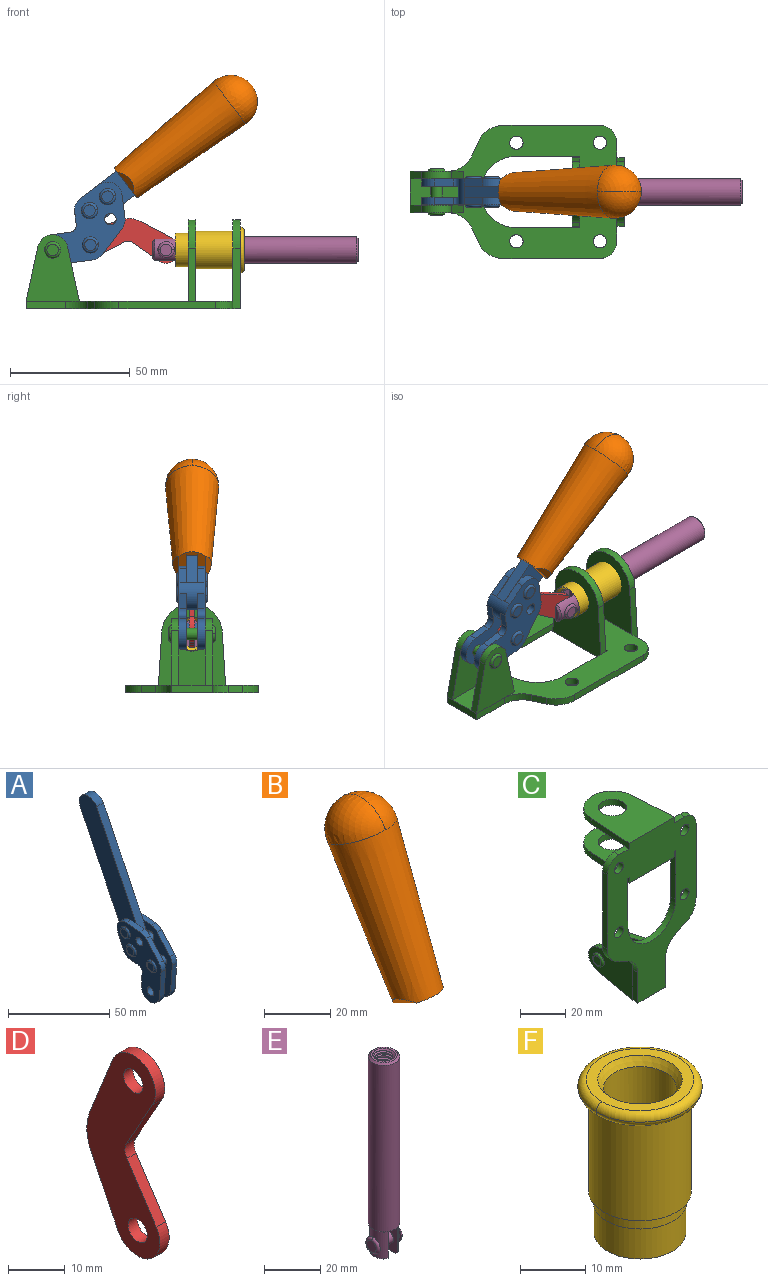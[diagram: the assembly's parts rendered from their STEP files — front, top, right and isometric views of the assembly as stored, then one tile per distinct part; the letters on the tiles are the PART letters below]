
ASSEMBLY  parts=6 mates=6
PART A: 59 faces, bbox 12.9x60.2x99.6 mm
  f0: torus R=2.39mm, axis (-1,0,0), area 14.9mm2, adj f20,f43,f51
  f1: torus R=2.39mm, axis (-1,0,0), area 14.9mm2, adj f19,f42,f51
  f2: torus R=2.39mm, axis (-1,0,0), area 14.9mm2, adj f18,f35,f51
  f3: torus R=2.39mm, axis (-1,0,0), area 14.9mm2, adj f14,f17,f23
  f4: torus R=2.39mm, axis (-1,0,0), area 14.9mm2, adj f13,f16,f23
  f5: torus R=2.39mm, axis (-1,0,0), area 14.9mm2, adj f12,f15,f23
  f6: cylinder r=2.39mm len=4.78mm, axis (1,0,0), area 46.5mm2, adj f48,f50,f51
  f7: cylinder r=2.39mm len=4.78mm, axis (1,0,0), area 46.5mm2, adj f50,f51
  f8: cylinder r=6.35mm len=12.68mm, axis (1,0,0), area 61.8mm2, adj f38,f39,f50,f51
  f9: cylinder r=2.39mm len=4.78mm, axis (-1,0,0), area 70.5mm2, adj f46,f50
  f10: cylinder r=2.39mm len=4.78mm, axis (-1,0,0), area 46.5mm2, adj f23,f45,f46
  f11: cylinder r=2.39mm len=4.78mm, axis (-1,0,0), area 46.5mm2, adj f23,f46
  f12: plane 4.78x4.78mm, normal (1,0,0), area 17.9mm2, adj f5,f15
  f13: plane 4.78x4.78mm, normal (1,0,0), area 17.9mm2, adj f4,f16
  f14: plane 4.78x4.78mm, normal (1,0,0), area 17.9mm2, adj f3,f17
  f15: torus R=2.39mm, axis (-1,0,0), area 14.9mm2, adj f5,f12,f23
  f16: torus R=2.39mm, axis (-1,0,0), area 14.9mm2, adj f4,f13,f23
  f17: torus R=2.39mm, axis (-1,0,0), area 14.9mm2, adj f3,f14,f23
  f18: plane 4.78x4.78mm, normal (-1,0,0), area 17.9mm2, adj f2,f35
  f19: plane 4.78x4.78mm, normal (-1,0,0), area 17.9mm2, adj f1,f42
  f20: plane 4.78x4.78mm, normal (-1,0,0), area 17.9mm2, adj f0,f43
  f21: plane 2.26x0.2mm, normal (1,0,0), area 0.2mm2, adj f31,f44
  f22: plane 2.26x0.2mm, normal (-1,0,0), area 0.2mm2, adj f41,f44
  f23: plane 39.37x30.77mm, normal (1,0,0), area 565.5mm2, adj f3,f4,f5,f10,f11,f15,f16,f17
  f24: cylinder r=6.1mm len=4.15mm, axis (-1,0,0), area 14.7mm2, adj f23,f25,f32,f46
  f25: plane 10.25x9.01mm, normal (0,-0.75,0.66), area 42.3mm2, adj f23,f24,f26,f46
  f26: cylinder r=6.35mm len=4.64mm, axis (-1,0,0), area 15.6mm2, adj f23,f25,f27,f46
  f27: plane 15.84x3.1mm, normal (0,-1,-0.07), area 49.2mm2, adj f23,f26,f28,f46
  f28: cylinder r=6.35mm len=12.68mm, axis (-1,0,0), area 61.8mm2, adj f23,f27,f29,f46
  f29: plane 8.11x3.1mm, normal (0,1,0.07), area 25.2mm2, adj f23,f28,f30,f46
  f30: cylinder r=3.05mm len=3.25mm, axis (-1,0,0), area 14.8mm2, adj f23,f29,f31,f46
  f31: plane 5.99x3.1mm, normal (0,0.07,-1), area 18.6mm2, adj f21,f23,f30,f44,f46
  f32: plane 9.5x3.1mm, normal (0,-0.07,1), area 29.5mm2, adj f23,f24,f33,f46,f47
  f33: cylinder r=6.1mm len=8.63mm, axis (-1,0,0), area 39.1mm2, adj f23,f32,f34,f47
  f34: plane 8.65x3.96mm, normal (0,0.91,-0.42), area 29.5mm2, adj f23,f33,f44,f47
  f35: torus R=2.39mm, axis (-1,0,0), area 14.9mm2, adj f2,f18,f51
  f36: plane 10.25x9.01mm, normal (0,-0.75,0.66), area 42.3mm2, adj f37,f49,f50,f51
  f37: cylinder r=6.35mm len=4.64mm, axis (1,0,0), area 15.6mm2, adj f36,f38,f50,f51
  f38: plane 15.84x3.1mm, normal (0,-1,-0.07), area 49.2mm2, adj f8,f37,f50,f51
  f39: plane 8.11x3.1mm, normal (0,1,0.07), area 25.2mm2, adj f8,f40,f50,f51
  f40: cylinder r=3.05mm len=3.25mm, axis (1,0,0), area 14.8mm2, adj f39,f41,f50,f51
  f41: plane 5.99x3.1mm, normal (0,0.07,-1), area 18.6mm2, adj f22,f40,f44,f50,f51
  f42: torus R=2.39mm, axis (-1,0,0), area 14.9mm2, adj f1,f19,f51
  f43: torus R=2.39mm, axis (-1,0,0), area 14.9mm2, adj f0,f20,f51
  f44: cylinder r=6.35mm len=12.12mm, axis (-1,0,0), area 128.9mm2, adj f21,f22,f23,f31,f34,f41,f46,f47
  f45: plane 2.65x1.35mm, normal (1,0,0), area 1mm2, adj f10,f55
  f46: plane 39.08x20.42mm, normal (-1,0,0), area 412.5mm2, adj f9,f10,f11,f24,f25,f26,f27,f28
  f47: plane 77.62x39.82mm, normal (1,0,0), area 850mm2, adj f32,f33,f34,f44,f53,f54,f55
  f48: plane 2.65x1.35mm, normal (-1,0,0), area 1mm2, adj f6,f55
  f49: cylinder r=6.1mm len=4.15mm, axis (1,0,0), area 14.7mm2, adj f36,f50,f51,f56
  f50: plane 39.08x20.42mm, normal (1,0,0), area 412.5mm2, adj f6,f7,f8,f9,f36,f37,f38,f39
  f51: plane 39.37x30.77mm, normal (-1,0,0), area 565.5mm2, adj f0,f1,f2,f6,f7,f8,f35,f36
  f52: plane 8.65x3.96mm, normal (0,0.91,-0.42), area 29.5mm2, adj f44,f51,f57,f58
  f53: plane 68.49x33.4mm, normal (0,0.9,-0.44), area 358.1mm2, adj f44,f47,f54,f58
  f54: cylinder r=6.35mm len=12.06mm, axis (1,0,0), area 93.7mm2, adj f47,f53,f55,f58
  f55: plane 68.49x33.4mm, normal (0,-0.9,0.44), area 358.1mm2, adj f44,f45,f46,f47,f48,f50,f54,f58
  f56: plane 9.5x3.1mm, normal (0,-0.07,1), area 29.5mm2, adj f49,f50,f51,f57,f58
  f57: cylinder r=6.1mm len=8.63mm, axis (1,0,0), area 39.1mm2, adj f51,f52,f56,f58
  f58: plane 77.62x39.82mm, normal (-1,0,0), area 850mm2, adj f44,f52,f53,f54,f55,f56,f57
PART B: 11 faces, bbox 22.3x42.6x64.5 mm
  f0: sphere r=11.13mm, area 411.4mm2, adj f1,f8
  f1: cone r=11.11mm half-angle=3.3deg, axis (0,0.44,0.9), area 3251.8mm2, adj f0,f7,f8,f9,f10
  f2: cylinder r=6.16mm len=11.7mm, axis (1,0,0), area 89.5mm2, adj f3,f4,f5,f6
  f3: plane 60.23x36.75mm, normal (-1,0,0), area 763.6mm2, adj f2,f4,f6,f10
  f4: plane 51.37x25.05mm, normal (0,0.9,-0.44), area 264.2mm2, adj f2,f3,f5,f10
  f5: plane 60.23x36.75mm, normal (1,0,0), area 763.6mm2, adj f2,f4,f6,f10
  f6: plane 51.37x25.05mm, normal (0,-0.9,0.44), area 264.2mm2, adj f2,f3,f5,f10
  f7: plane 9.95x5.95mm, normal (0.71,-0.31,-0.64), area 25.8mm2, adj f1,f10
  f8: sphere r=11.13mm, area 411.4mm2, adj f0,f1
  f9: plane 9.95x5.95mm, normal (-0.71,-0.31,-0.64), area 25.8mm2, adj f1,f10
  f10: plane 14.27x11.38mm, normal (0,-0.44,-0.9), area 106.7mm2, adj f1,f3,f4,f5,f6,f7,f9
PART C: 55 faces, bbox 55.7x37.4x89.8 mm
  f0: torus R=2.41mm, axis (-1,0,0), area 15mm2, adj f11,f15,f25
  f1: torus R=2.41mm, axis (-1,0,0), area 15mm2, adj f10,f12,f22
  f2: cylinder r=2.78mm len=5.56mm, axis (0,-1,0), area 54.2mm2, adj f30,f54
  f3: cylinder r=14.99mm len=29.97mm, axis (0,-1,0), area 145.9mm2, adj f30,f49,f53,f54
  f4: cylinder r=2.78mm len=5.56mm, axis (0,-1,0), area 54.2mm2, adj f30,f54
  f5: cylinder r=2.78mm len=5.56mm, axis (0,-1,0), area 54.2mm2, adj f30,f54
  f6: cylinder r=2.78mm len=5.56mm, axis (0,-1,0), area 54.2mm2, adj f30,f54
  f7: cylinder r=6.35mm len=12.7mm, axis (0,0,1), area 123.6mm2, adj f27,f51
  f8: cylinder r=6.35mm len=12.7mm, axis (0,0,-1), area 124.7mm2, adj f21,f35
  f9: cylinder r=2.41mm len=11.18mm, axis (-1,0,0), area 169.4mm2, adj f16,f19
  f10: plane 4.83x4.83mm, normal (1,0,0), area 18.3mm2, adj f1,f12
  f11: plane 4.83x4.83mm, normal (-1,0,0), area 18.3mm2, adj f0,f15
  f12: torus R=2.41mm, axis (-1,0,0), area 15mm2, adj f1,f10,f22
  f13: cylinder r=6.35mm len=12.41mm, axis (1,0,0), area 53.4mm2, adj f18,f19,f22,f23
  f14: cylinder r=6.35mm len=12.41mm, axis (-1,0,0), area 53.4mm2, adj f16,f17,f24,f25
  f15: torus R=2.41mm, axis (-1,0,0), area 15mm2, adj f0,f11,f25
  f16: plane 27.86x22.35mm, normal (1,0,0), area 425.4mm2, adj f9,f14,f17,f24,f30
  f17: plane 22.86x4.97mm, normal (0,0.21,0.98), area 72.5mm2, adj f14,f16,f25,f30
  f18: plane 22.86x4.97mm, normal (0,0.21,0.98), area 72.5mm2, adj f13,f19,f22,f30
  f19: plane 27.86x22.35mm, normal (-1,0,0), area 425.4mm2, adj f9,f13,f18,f23,f30
  f20: cylinder r=12.7mm len=25.35mm, axis (0,0,-1), area 119.8mm2, adj f21,f34,f35,f36
  f21: plane 34.21x28.07mm, normal (0,0,-1), area 702.4mm2, adj f8,f20,f30,f34,f36
  f22: plane 27.96x22.45mm, normal (1,0,0), area 407.2mm2, adj f1,f12,f13,f18,f23,f30,f42,f43
  f23: plane 22.86x4.97mm, normal (0,0.21,-0.98), area 72.5mm2, adj f13,f19,f22,f44
  f24: plane 22.86x4.97mm, normal (0,0.21,-0.98), area 72.5mm2, adj f14,f16,f25,f44
  f25: plane 27.86x22.35mm, normal (-1,0,0), area 407.1mm2, adj f0,f14,f15,f17,f24,f30,f45,f46
  f26: plane 3.1x0.95mm, normal (0,0,-1), area 2.7mm2, adj f30,f49,f50,f54
  f27: plane 34.21x28.07mm, normal (0,0,1), area 702.4mm2, adj f7,f28,f30,f50,f52
  f28: cylinder r=12.7mm len=25.35mm, axis (0,0,1), area 118.8mm2, adj f27,f50,f51,f52
  f29: plane 3.1x0.95mm, normal (0,0,-1), area 2.7mm2, adj f30,f52,f53,f54
  f30: plane 86.54x55.63mm, normal (0,1,0), area 2362.9mm2, adj f2,f3,f4,f5,f6,f16,f17,f18
  f31: plane 40.56x3.1mm, normal (-1,0,0), area 125.7mm2, adj f30,f32,f48,f54
  f32: cylinder r=7.11mm len=7.11mm, axis (0,-1,0), area 34.6mm2, adj f30,f31,f33,f54
  f33: plane 6.67x3.1mm, normal (0,0,1), area 20.4mm2, adj f30,f32,f34,f54
  f34: plane 25.39x3.13mm, normal (-1,0.06,0), area 79.5mm2, adj f20,f21,f33,f35,f54
  f35: plane 37.31x28.45mm, normal (0,0,1), area 789.9mm2, adj f8,f20,f34,f36,f54
  f36: plane 25.39x3.13mm, normal (1,0.06,0), area 79.5mm2, adj f20,f21,f35,f37,f54
  f37: plane 6.67x3.1mm, normal (0,0,1), area 20.4mm2, adj f30,f36,f38,f54
  f38: cylinder r=7.11mm len=7.11mm, axis (0,-1,0), area 34.6mm2, adj f30,f37,f39,f54
  f39: plane 40.56x3.1mm, normal (1,0,0), area 125.7mm2, adj f30,f38,f40,f54
  f40: cylinder r=11.18mm len=10.16mm, axis (0,-1,0), area 39.5mm2, adj f30,f39,f41,f54
  f41: plane 6.09x3.1mm, normal (0.42,0,-0.91), area 20.8mm2, adj f30,f40,f42,f54
  f42: cylinder r=11.18mm len=9.41mm, axis (0,-1,0), area 37.2mm2, adj f22,f30,f41,f43,f54
  f43: plane 16.5x3.1mm, normal (1,0,0), area 51.1mm2, adj f22,f42,f44,f54
  f44: plane 17.37x3.1mm, normal (0,0,-1), area 53.8mm2, adj f23,f24,f30,f43,f45,f54
  f45: plane 16.5x3.1mm, normal (-1,0,0), area 51.1mm2, adj f25,f44,f46,f54
  f46: cylinder r=11.18mm len=9.41mm, axis (0,-1,0), area 37.2mm2, adj f25,f30,f45,f47,f54
  f47: plane 6.09x3.1mm, normal (-0.42,0,-0.91), area 20.8mm2, adj f30,f46,f48,f54
  f48: cylinder r=11.18mm len=10.16mm, axis (0,-1,0), area 39.5mm2, adj f30,f31,f47,f54
  f49: plane 26.54x3.1mm, normal (-1,0,0), area 82.3mm2, adj f3,f26,f30,f54
  f50: plane 25.39x3.1mm, normal (1,0.06,0), area 78.8mm2, adj f26,f27,f28,f51,f54
  f51: plane 37.31x28.45mm, normal (0,0,-1), area 789.9mm2, adj f7,f28,f50,f52,f54
  f52: plane 25.39x3.1mm, normal (-1,0.06,0), area 78.8mm2, adj f27,f28,f29,f51,f54
  f53: plane 26.54x3.1mm, normal (1,0,0), area 82.3mm2, adj f3,f29,f30,f54
  f54: plane 89.66x55.63mm, normal (0,-1,0), area 2678.5mm2, adj f2,f3,f4,f5,f6,f26,f29,f31
PART D: 12 faces, bbox 2.3x18.2x42.8 mm
  f0: cylinder r=2.4mm len=4.8mm, axis (1,0,0), area 34.9mm2, adj f4,f11
  f1: cylinder r=10.41mm len=8.47mm, axis (1,0,0), area 20.2mm2, adj f4,f9,f10,f11
  f2: cylinder r=3.05mm len=3.16mm, axis (1,0,0), area 7.7mm2, adj f4,f6,f7,f11
  f3: cylinder r=2.4mm len=4.8mm, axis (1,0,0), area 34.9mm2, adj f4,f11
  f4: plane 42.81x18.23mm, normal (-1,0,0), area 414.1mm2, adj f0,f1,f2,f3,f5,f6,f7,f8
  f5: cylinder r=5.54mm len=10.67mm, axis (1,0,0), area 41.8mm2, adj f4,f6,f10,f11
  f6: plane 11.66x6.53mm, normal (0,-0.87,-0.49), area 30.9mm2, adj f2,f4,f5,f11
  f7: plane 11.17x7.33mm, normal (0,-0.84,0.55), area 30.9mm2, adj f2,f4,f8,f11
  f8: cylinder r=5.54mm len=10.51mm, axis (1,0,0), area 41.8mm2, adj f4,f7,f9,f11
  f9: plane 13.67x6.67mm, normal (0,0.9,-0.44), area 35.1mm2, adj f1,f4,f8,f11
  f10: plane 14.1x5.7mm, normal (0,0.93,0.37), area 35.1mm2, adj f1,f4,f5,f11
  f11: plane 42.81x18.23mm, normal (1,0,0), area 414.1mm2, adj f0,f1,f2,f3,f5,f6,f7,f8
PART E: 48 faces, bbox 12.6x11.1x86.1 mm
  f0: torus R=2.41mm, axis (-1,0,0), area 15mm2, adj f30,f32,f34
  f1: torus R=2.41mm, axis (-1,0,0), area 15mm2, adj f29,f31,f33
  f2: cylinder r=5.54mm len=72.39mm, axis (0,0,1), area 2518.5mm2, adj f3,f4,f42,f43
  f3: cone r=5.54mm half-angle=45deg, axis (0,0,1), area 7.6mm2, adj f2,f5,f41
  f4: cone r=5.54mm half-angle=45deg, axis (0,0,-1), area 34.9mm2, adj f2,f39
  f5: cylinder r=5.08mm len=11.48mm, axis (0,0,1), area 108.3mm2, adj f3,f7,f8,f41
  f6: cylinder r=2.41mm len=4.83mm, axis (-1,0,0), area 71.2mm2, adj f40,f41
  f7: cylinder r=2.41mm len=4.83mm, axis (-1,0,0), area 7.6mm2, adj f5,f34
  f8: cone r=5.08mm half-angle=45deg, axis (0,0,1), area 10.6mm2, adj f5,f37,f41
  f9: cone r=3.98mm half-angle=45deg, axis (0,0,1), area 17.6mm2, adj f27,f39,f45,f46,f47
  f10: cylinder r=2.41mm len=4.83mm, axis (-1,0,0), area 7.6mm2, adj f33,f38
  f11: cylinder r=3.2mm len=6.4mm, axis (0,0,1), area 78.4mm2, adj f12,f28,f44,f45,f47
  f12: cylinder r=3.2mm len=6.4mm, axis (0,0,1), area 10.5mm2, adj f11,f13,f45,f47
  f13: cylinder r=3.2mm len=6.4mm, axis (0,0,1), area 10.5mm2, adj f12,f14,f45,f47
  f14: cylinder r=3.2mm len=6.4mm, axis (0,0,1), area 10.5mm2, adj f13,f15,f45,f47
  f15: cylinder r=3.2mm len=6.4mm, axis (0,0,1), area 10.5mm2, adj f14,f16,f45,f47
  f16: cylinder r=3.2mm len=6.4mm, axis (0,0,1), area 10.5mm2, adj f15,f17,f45,f47
  f17: cylinder r=3.2mm len=6.4mm, axis (0,0,1), area 10.5mm2, adj f16,f18,f45,f47
  f18: cylinder r=3.2mm len=6.4mm, axis (0,0,1), area 10.5mm2, adj f17,f19,f45,f47
  f19: cylinder r=3.2mm len=6.4mm, axis (0,0,1), area 10.5mm2, adj f18,f20,f45,f47
  f20: cylinder r=3.2mm len=6.4mm, axis (0,0,1), area 10.5mm2, adj f19,f21,f45,f47
  f21: cylinder r=3.2mm len=6.4mm, axis (0,0,1), area 10.5mm2, adj f20,f22,f45,f47
  f22: cylinder r=3.2mm len=6.4mm, axis (0,0,1), area 10.5mm2, adj f21,f23,f45,f47
  f23: cylinder r=3.2mm len=6.4mm, axis (0,0,1), area 10.5mm2, adj f22,f24,f45,f47
  f24: cylinder r=3.2mm len=6.4mm, axis (0,0,1), area 10.5mm2, adj f23,f25,f45,f47
  f25: cylinder r=3.2mm len=6.4mm, axis (0,0,1), area 10.5mm2, adj f24,f26,f45,f47
  f26: cylinder r=3.2mm len=6.4mm, axis (0,0,1), area 10.5mm2, adj f25,f27,f45,f47
  f27: cylinder r=3.2mm len=6.4mm, axis (0,0,1), area 7.4mm2, adj f9,f26,f45,f47
  f28: cone r=3.2mm half-angle=60deg, axis (0,0,1), area 37.2mm2, adj f11
  f29: plane 4.83x4.83mm, normal (-1,0,0), area 18.3mm2, adj f1,f31
  f30: plane 4.83x4.83mm, normal (1,0,0), area 18.3mm2, adj f0,f32
  f31: torus R=2.41mm, axis (-1,0,0), area 15mm2, adj f1,f29,f33
  f32: torus R=2.41mm, axis (-1,0,0), area 15mm2, adj f0,f30,f34
  f33: plane 6.83x6.83mm, normal (1,0,0), area 18.3mm2, adj f1,f10,f31
  f34: plane 6.83x6.83mm, normal (-1,0,0), area 18.3mm2, adj f0,f7,f32
  f35: cone r=5.08mm half-angle=45deg, axis (0,0,1), area 10.6mm2, adj f36,f38,f40
  f36: plane 7.25x1.97mm, normal (0,0,-1), area 10mm2, adj f35,f40
  f37: plane 7.25x1.97mm, normal (0,0,-1), area 10mm2, adj f8,f41
  f38: cylinder r=5.08mm len=11.48mm, axis (0,0,1), area 108.3mm2, adj f10,f35,f40,f42
  f39: plane 9.55x9.55mm, normal (0,0,1), area 22mm2, adj f4,f9
  f40: plane 12.76x10.09mm, normal (1,0,0), area 95.7mm2, adj f6,f35,f36,f38,f42,f43
  f41: plane 12.76x10.09mm, normal (-1,0,0), area 95.7mm2, adj f3,f5,f6,f8,f37,f43
  f42: cone r=5.54mm half-angle=45deg, axis (0,0,1), area 7.6mm2, adj f2,f38,f40
  f43: plane 11.07x4.7mm, normal (0,0,-1), area 50.4mm2, adj f2,f40,f41
  f44: plane 0.89x0.62mm, normal (-1,0,0), area 0.3mm2, adj f11,f45,f46,f47
  f45: bspline ~24.8x7.63mm, area 266.6mm2, adj f9,f11,f12,f13,f14,f15,f16,f17
  f46: bspline ~24.87x7.63mm, area 73.6mm2, adj f9,f44,f45,f47
  f47: bspline ~24.98x7.63mm, area 272.5mm2, adj f9,f11,f12,f13,f14,f15,f16,f17
PART F: 15 faces, bbox 20.6x20.6x28.7 mm
  f0: torus R=8.26mm, axis (0,0,1), area 56.8mm2, adj f1,f10,f12
  f1: torus R=8.26mm, axis (0,0,1), area 56.8mm2, adj f0,f6,f13
  f2: cylinder r=5.59mm len=25.91mm, axis (0,0,1), area 909.6mm2, adj f3,f4
  f3: cone r=6.86mm half-angle=45deg, axis (0,0,-1), area 70.2mm2, adj f2,f14
  f4: cone r=6.47mm half-angle=30deg, axis (0,0,1), area 66.7mm2, adj f2,f13
  f5: cylinder r=7.04mm len=14.07mm, axis (0,0,1), area 252.6mm2, adj f11,f14
  f6: torus R=8.26mm, axis (0,0,1), area 56.8mm2, adj f1,f12,f13
  f7: cylinder r=7.16mm len=14.33mm, axis (0,0,1), area 91.5mm2, adj f9,f11
  f8: cylinder r=7.86mm len=18.42mm, axis (0,0,1), area 909.6mm2, adj f9,f10
  f9: plane 15.72x15.72mm, normal (0,0,-1), area 33mm2, adj f7,f8
  f10: plane 16.51x16.51mm, normal (0,0,-1), area 19.9mm2, adj f0,f8,f12
  f11: plane 14.33x14.33mm, normal (0,0,-1), area 5.7mm2, adj f5,f7
  f12: torus R=8.26mm, axis (0,0,1), area 56.8mm2, adj f0,f6,f10
  f13: plane 16.51x16.51mm, normal (0,0,1), area 82.7mm2, adj f1,f4,f6
  f14: plane 14.07x14.07mm, normal (0,0,-1), area 7.8mm2, adj f3,f5
PLACE A rot(axis=(0.53,0.53,0.65),113.6deg) t=(-5.14,0,6.95)mm
PLACE B rot(axis=(-0.22,0.22,-0.95),93deg) t=(-53.74,-0.04,70.09)mm
PLACE C rot(axis=(0.58,0.58,0.58),120deg) t=(-9.43,0,0)mm fixed
PLACE D rot(axis=(0.6,0.6,0.54),123.4deg) t=(-11.98,0,1.68)mm
PLACE E rot(axis=(0.58,0.58,0.58),120deg) t=(-9.58,0,0)mm
PLACE F rot(axis=(0.71,0,0.71),180deg) t=(-10.45,24.61,24.61)mm
MATE revolute D.f3 <-> A.f4  axis (0,1,0) through (-25.79,0,26.71)mm
MATE slider E.f2 <-> F.f2  axis (1,0,0) through (49.2,0,24.61)mm
MATE revolute A.f7 <-> C.f0  axis (0,1,0) through (-41.52,0,24.61)mm
MATE fastened A.f54 <-> B.f2  axis (0,-1,0) through (34.25,-2.35,87.54)mm
MATE revolute E.f6 <-> D.f5  axis (0,-1,0) through (5.89,0,24.61)mm
MATE fastened F.f2 <-> C.f7  axis (-1,0,0) through (36.96,0,24.61)mm
